# Revit family: ALBA_R100ExSWxxSF
name_source: partatom
category: Leuchten
units: mm (PartAtom-declared; Revit-internal decimal feet)

## family parameters
Basisbauteil = Fläche
Beim Laden mit Abzugskörper schneiden = Nein
Bemaßung runder Anschluss = Durchmesser verwenden
Gemeinsam genutzt = Nein
Lichtquelle = Ja
OmniClass-Nummer = 23.80.70.11
OmniClass-Titel = Luminaries for Internal Lighting
Raumberechnungspunkt = Nein
Teiletyp = Normal

## types (8) — shared parameters
Baugruppenkennzeichen = D5020200
Datei für fotometrisches Netz = Master_ALBA_R100E_SW_Diffusor.IES
Emissionsform beim Rendern sichtbar = Nein
Farbfilter = 16777215
Farbtemperaturverschiebung bei Dämpfen der Lampe = <Keine Auswahl>
Hersteller = RIDI Leuchten GmbH
Lampe = LED
Neigungswinkel = 90.00°
Scheinlast = 15 VA
URL = www.ridi.de
Von Kreisdurchmesser aussenden = 86 mm  [stored 0.282152 ft]
brand = RIDI
conformity mark = CE
electrical safety class = 2
height = 84 mm  [stored 0.275591 ft]
ingress protection (IP) code = IP20
length = 112 mm  [stored 0.367454 ft]
nominal frequency = 50-60Hz
nominal voltage = 230
rated input power = 15
voltage type (AC, DC, UC) = AC
weight = 0.43 kg
width = 112 mm  [stored 0.367454 ft]
zero-valued in all types: Vorgabe-Ansicht

## per-type parameters (varying)
| type | Modell |
| ALBA R100E NDSW930SF0070OS | 0322123 |
| ALBA R100E NDSW940SF0080OS | 0322124 |
| ALBA R100E DASW930SF0070OS | 0332123 |
| ALBA R100E DASW940SF0080OS | 0332124 |
| ALBA R100E NDSW830SF0090OS | 0322316 |
| ALBA R100E NDSW840SF0090OS | 0322317 |
| ALBA R100E DASW830SF0090OS | 0332316 |
| ALBA R100E DASW840SF0090OS | 0332317 |

note: column(s) folded — value = type name in every type: product name

note: [stored X ft] marks values corroborated as IEEE doubles in the binary element streams (Revit-internal decimal feet)
